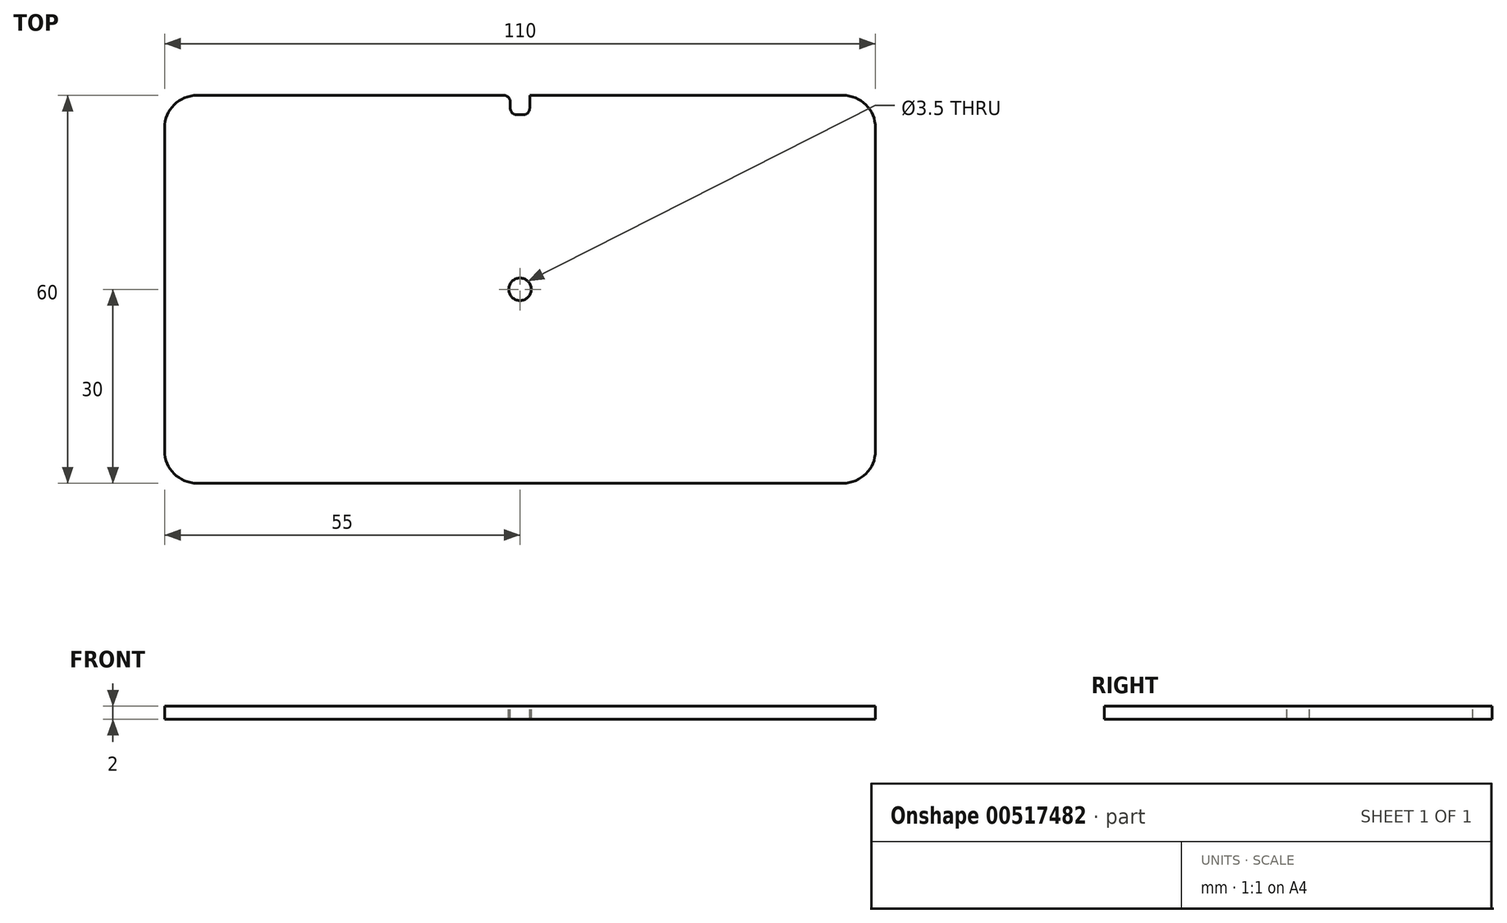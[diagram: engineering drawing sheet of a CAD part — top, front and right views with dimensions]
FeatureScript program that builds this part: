
annotation { "Feature Type Name" : "Feature", "Feature Type Description" : "" }
export const myFeature = defineFeature(function(context is Context, id is Id, definition is map)
    precondition{}
    {
        {
            var Q0;
            Q0=qCreatedBy(makeId("Top.planeOp"),FACE);
            var sketch = newSketch(context, id + "F0", { "sketchPlane" : qUnion([Q0])});
            skLineSegment(sketch, "E0.bottom", {"start": v(55, 30) * mm, "end": v(-55, 30) * mm});
            skLineSegment(sketch, "E0.top", {"start": v(55, -30) * mm, "end": v(-55, -30) * mm});
            skLineSegment(sketch, "E0.left", {"start": v(55, 30) * mm, "end": v(55, -30) * mm});
            skLineSegment(sketch, "E0.right", {"start": v(-55, 30) * mm, "end": v(-55, -30) * mm});
            skPoint(sketch, "E0.middle", {"position": v(0, 0) * mm});
            skSolve(sketch);
        }
        {
            var Q0;
            Q0 = qSketchRegion(id + "F0", true);
            extrude(context, id + "F1", {"entities" : qUnion([Q0]), "depth" : 2 * mm, "offsetDistance" : 25 * mm});
        }
        {
            var Q0;
            Q0=makeQuery(id+"F1.opExtrude","SWEPT_EDGE",EDGE,{"disambiguationData":[OSD([sQuery(id+"F0.wireOp",EDGE,"E0.top"),sQuery(id+"F0.wireOp",EDGE,"E0.left")])]});
            var Q1;
            Q1=makeQuery(id+"F1.opExtrude","SWEPT_EDGE",EDGE,{"disambiguationData":[OSD([sQuery(id+"F0.wireOp",EDGE,"E0.bottom"),sQuery(id+"F0.wireOp",EDGE,"E0.left")])]});
            var Q2;
            Q2=makeQuery(id+"F1.opExtrude","SWEPT_EDGE",EDGE,{"disambiguationData":[OSD([sQuery(id+"F0.wireOp",EDGE,"E0.bottom"),sQuery(id+"F0.wireOp",EDGE,"E0.right")])]});
            var Q3;
            Q3=makeQuery(id+"F1.opExtrude","SWEPT_EDGE",EDGE,{"disambiguationData":[OSD([sQuery(id+"F0.wireOp",EDGE,"E0.top"),sQuery(id+"F0.wireOp",EDGE,"E0.right")])]});
            fillet(context, id + "F2", {"entities" : qUnion([Q0, Q1, Q2, Q3]), "radius" : 5 * mm, "tangentPropagation" : true, "allowEdgeOverflow" : false});
        }
        {
            var Q0;
            Q0=makeQuery(id+"F1.opExtrude","CAP_FACE",FACE,{"disambiguationData":[OSD([sQuery(id+"F0.wireOp",EDGE,"E0.bottom"),sQuery(id+"F0.wireOp",EDGE,"E0.top"),sQuery(id+"F0.wireOp",EDGE,"E0.left"),sQuery(id+"F0.wireOp",EDGE,"E0.right")])],"isStart":false});
            var sketch = newSketch(context, id + "F3", { "sketchPlane" : qUnion([Q0])});
            skLineSegment(sketch, "E1.bottom", {"start": v(1.5, 30) * mm, "end": v(-1.5, 30) * mm});
            skLineSegment(sketch, "E1.top", {"start": v(1.5, 27) * mm, "end": v(-1.5, 27) * mm});
            skLineSegment(sketch, "E1.left", {"start": v(1.5, 30) * mm, "end": v(1.5, 27) * mm});
            skLineSegment(sketch, "E1.right", {"start": v(-1.5, 30) * mm, "end": v(-1.5, 27) * mm});
            skPoint(sketch, "E1.middle", {"position": v(0, 28.5) * mm});
            skSolve(sketch);
        }
        {
            var Q0;
            Q0 = qSketchRegion(id + "F3", true);
            extrude(context, id + "F4", {"entities" : qUnion([Q0]), "operationType" : NewBodyOperationType.REMOVE, "oppositeDirection" : true, "depth" : 25 * mm, "offsetDistance" : 25 * mm});
        }
        {
            var Q0;
            Q0=makeQuery(id+"F4.boolean.opBoolean","COPY",EDGE,{"derivedFrom":makeQuery(id+"F4.opExtrude","SWEPT_EDGE",EDGE,{"disambiguationData":[OSD([sQuery(id+"F0.wireOp",EDGE,"E0.bottom"),sQuery(id+"F3.wireOp",EDGE,"E1.bottom"),sQuery(id+"F3.wireOp",EDGE,"E1.right")])]})});
            var Q1;
            Q1=makeQuery(id+"F4.boolean.opBoolean","COPY",EDGE,{"derivedFrom":makeQuery(id+"F4.opExtrude","SWEPT_EDGE",EDGE,{"disambiguationData":[OSD([sQuery(id+"F3.wireOp",EDGE,"E1.top"),sQuery(id+"F3.wireOp",EDGE,"E1.right")])]})});
            var Q2;
            Q2=makeQuery(id+"F4.boolean.opBoolean","COPY",EDGE,{"derivedFrom":makeQuery(id+"F4.opExtrude","SWEPT_EDGE",EDGE,{"disambiguationData":[OSD([sQuery(id+"F3.wireOp",EDGE,"E1.top"),sQuery(id+"F3.wireOp",EDGE,"E1.left")])]})});
            var Q3;
            Q3=makeQuery(id+"F4.boolean.opBoolean","COPY",EDGE,{"derivedFrom":makeQuery(id+"F4.opExtrude","SWEPT_EDGE",EDGE,{"disambiguationData":[OSD([sQuery(id+"F0.wireOp",EDGE,"E0.bottom"),sQuery(id+"F3.wireOp",EDGE,"E1.bottom"),sQuery(id+"F3.wireOp",EDGE,"E1.left")])]})});
            fillet(context, id + "F5", {"entities" : qUnion([Q0, Q1, Q2, Q3]), "radius" : 1 * mm, "tangentPropagation" : true, "allowEdgeOverflow" : false});
        }
        {
            var Q0;
            Q0=makeQuery(id+"F1.opExtrude","CAP_FACE",FACE,{"disambiguationData":[OSD([sQuery(id+"F0.wireOp",EDGE,"E0.bottom"),sQuery(id+"F0.wireOp",EDGE,"E0.top"),sQuery(id+"F0.wireOp",EDGE,"E0.left"),sQuery(id+"F0.wireOp",EDGE,"E0.right")])],"isStart":false});
            var sketch = newSketch(context, id + "F6", { "sketchPlane" : qUnion([Q0])});
            skCircle(sketch, "E2", {"center": v(0, 0) * mm, "radius": 1.75 * mm});
            skSolve(sketch);
        }
        {
            var Q0;
            Q0 = qSketchRegion(id + "F6", true);
            extrude(context, id + "F7", {"entities" : qUnion([Q0]), "operationType" : NewBodyOperationType.REMOVE, "oppositeDirection" : true, "depth" : 25 * mm, "offsetDistance" : 25 * mm});
        }
    });
